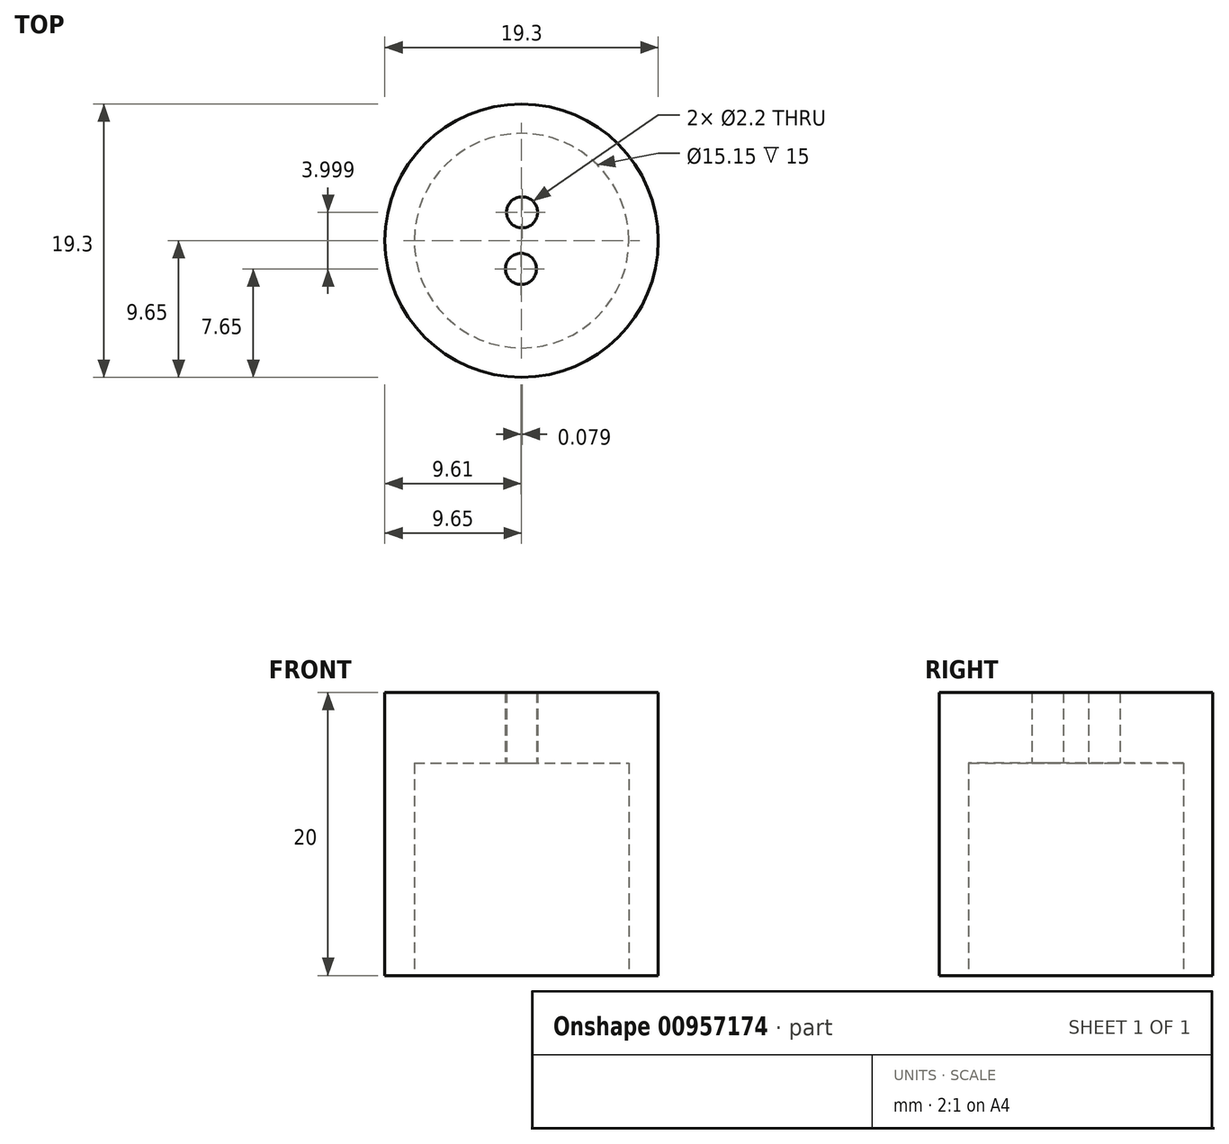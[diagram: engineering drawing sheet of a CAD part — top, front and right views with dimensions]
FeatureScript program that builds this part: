
annotation { "Feature Type Name" : "Feature", "Feature Type Description" : "" }
export const myFeature = defineFeature(function(context is Context, id is Id, definition is map)
    precondition{}
    {
        {
            var Q0;
            Q0=qCreatedBy(makeId("Top.planeOp"),FACE);
            var sketch = newSketch(context, id + "F0", { "sketchPlane" : qUnion([Q0])});
            skCircle(sketch, "E0", {"center": v(0, 0) * mm, "radius": 9.65 * mm});
            skCircle(sketch, "E1", {"center": v(0, 0) * mm, "radius": 7.58 * mm});
            skSolve(sketch);
        }
        {
            var Q0;
            Q0 = qSketchRegion(id + "F0", true);
            var Q1;
            Q1=makeQuery(id+"F0.imprint","IMPRINT",FACE,{"disambiguationData":[TD([[makeQuery(id+"F0.imprint","IMPRINT",EDGE,{"derivedFrom":sQuery(id+"F0.wireOp",EDGE,"E1")}),1.0]])]});
            extrude(context, id + "F1", {"entities" : qUnion([Q0, Q1]), "depth" : 20 * mm, "offsetDistance" : 25 * mm});
        }
        {
            var Q0;
            Q0=makeQuery(id+"F1.opExtrude","CAP_FACE",FACE,{"disambiguationData":[OSD([sQuery(id+"F0.wireOp",EDGE,"E0")])],"isStart":true});
            var sketch = newSketch(context, id + "F2", { "sketchPlane" : qUnion([Q0])});
            skCircle(sketch, "E2", {"center": v(0, 0) * mm, "radius": 7.58 * mm});
            skSolve(sketch);
        }
        {
            var Q0;
            Q0 = qSketchRegion(id + "F2", true);
            extrude(context, id + "F3", {"entities" : qUnion([Q0]), "operationType" : NewBodyOperationType.REMOVE, "oppositeDirection" : true, "depth" : 15 * mm, "offsetDistance" : 25 * mm});
        }
        {
            var Q0;
            Q0=makeQuery(id+"F3.boolean.opBoolean","COPY",FACE,{"derivedFrom":makeQuery(id+"F3.opExtrude","CAP_FACE",FACE,{"disambiguationData":[OSD([sQuery(id+"F2.wireOp",EDGE,"E2")])],"isStart":false})});
            var sketch = newSketch(context, id + "F4", { "sketchPlane" : qUnion([Q0])});
            skCircle(sketch, "E3", {"center": v(0, 0) * mm, "radius": 2 * mm, "construction": true});
            skCircle(sketch, "E4", {"center": v(-0.04, 2) * mm, "radius": 1.1 * mm});
            skCircle(sketch, "E5.1.0", {"center": v(0.04, -2) * mm, "radius": 1.1 * mm});
            skSolve(sketch);
        }
        {
            var Q0;
            Q0 = qSketchRegion(id + "F4", true);
            extrude(context, id + "F5", {"entities" : qUnion([Q0]), "operationType" : NewBodyOperationType.REMOVE, "endBound" : BoundingType.THROUGH_ALL, "oppositeDirection" : true, "depth" : 25 * mm, "offsetDistance" : 25 * mm});
        }
    });
